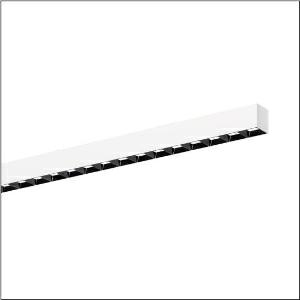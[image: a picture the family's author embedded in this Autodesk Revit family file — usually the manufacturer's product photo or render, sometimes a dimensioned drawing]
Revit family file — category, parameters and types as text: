
# Revit family: silica_r__21_51mx21dc4awb_19b2
name_source: partatom
category: Lighting Fixtures
units: mm (PartAtom-declared; Revit-internal decimal feet)

## family parameters
Cut with Voids When Loaded = No
Host = Face
Light Source = No
Part Type = Normal
Room Calculation Point = No
Round Connector Dimension = Use Diameter
Shared = No

## types (1)
- --- (1 x LED, 10800 lm, 64.8 W, 4000K)
    Apparent Load = 65 VA
    CIE Flux Codes = 87 99 100 100 100
    Color Rendering = 80
    Color Temperature = 4000K
    Default Elevation = 1800 mm
    Description = Silica® 21, office luminaire, primary light control with darklight reflector, of PMMA, black, CAT 2 (L<= 3000cd/m²), light emission: direct distribution, primary light characteristic: symmetric, installation type: surface-mounted, LED, rated luminous flux: 10.800lm, luminous efficacy: 167lm/W, light colour: 840, colour temperature: 4000K, with terminal, 3+2-pole, max. 2.5mm², mains connection: 220..240V, AC, 50/60Hz, rated input power: 64.8W, luminaire housing, of aluminium, traffic white (RAL 9016), length: 3.004mm, width: 53mm, height: 53mm, protection rating (complete): IP20, insulation class (complete): insulation class I (protective earthing), certification: CE, permissible operating ambient temperature: 0..+35°C, standard: EN 50419, packaging unit: 1 piece
    Height = 0 mm  [stored 0 ft]
    Lamp = 1 x LED
    Lamp Light Flux = 10800 lm
    Lamp Power = 64.8 W
    Lamp count = 1
    Length = 3004 mm
    Luminous efficacy = 167 lm/W
    Manufacturer = Siteco
    ModVariant = No
    Model = 51MX21DC4AWB
    Mounting Place = Ceiling
    Mounting Type = Recessed
    Number of Poles = 1
    OnlyDefault = Yes
    Power Factor = 1
    Product Name = Silica® 21
    Product group = office luminaire | ceiling recessed
    ProductGroupID = 401
    Protection Class = Protection class I
    Protection Degree = IP 20
    RLX_Detail_Level = 1
    RLX_Emergency_Light_Flux = 0 lm
    RLX_Emergency_Type = 0
    RLX_Emergency_Type_DB = No
    RlxData = <blob elided: 62545 chars, md5=f2b39de9>
    Socket = socket
    Standby Power = 0 W
    System Light Flux = 10800 lm
    System Power = 65 W
    Type Comments = factory setting: luminous flux: 100 % | dim-lin: 254 | 367 mA
    Type Image = l_1313592.jpg
    URL = http://relux.com
    VarID = @adj_072979
    Voltage = 0 V
    Weight = 0.00 kg
    Width = 53 mm

note: [stored X ft] marks values corroborated as IEEE doubles in the binary element streams (Revit-internal decimal feet)

## geometry (parser evidence)
native form markers: Blend x4, Sweep x9
no freeform markers — native parametric forms only
